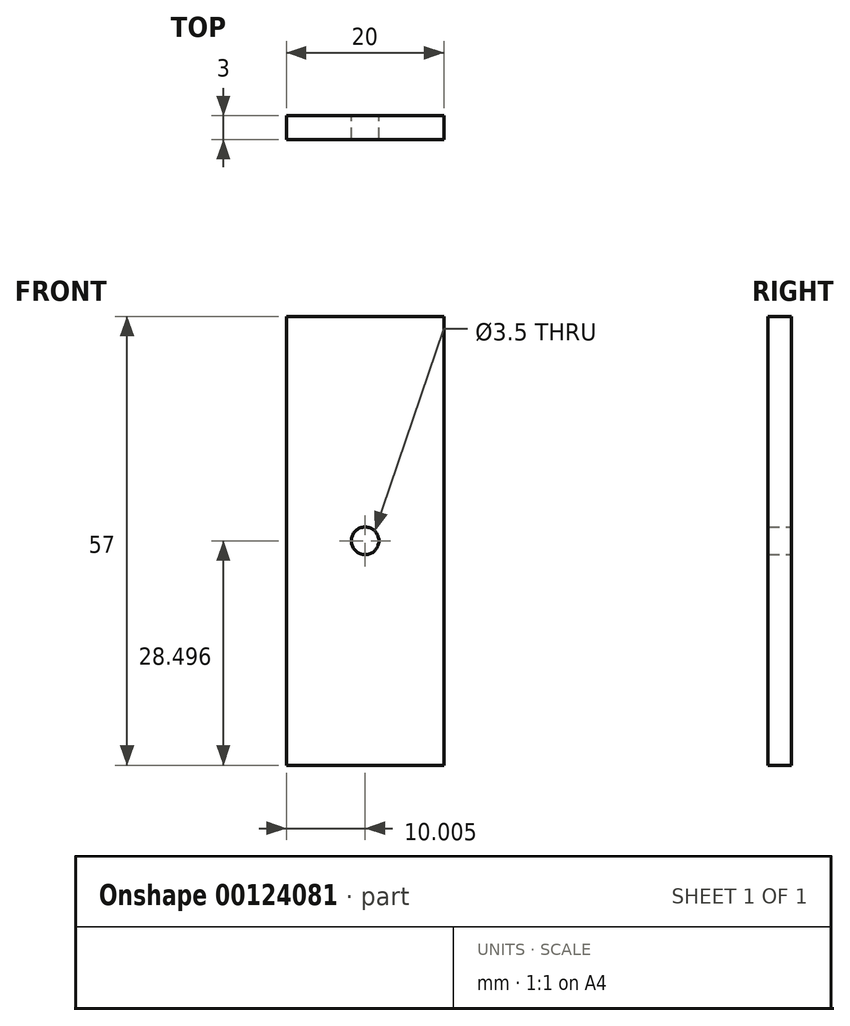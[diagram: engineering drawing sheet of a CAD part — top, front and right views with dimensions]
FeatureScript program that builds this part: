
annotation { "Feature Type Name" : "Feature", "Feature Type Description" : "" }
export const myFeature = defineFeature(function(context is Context, id is Id, definition is map)
    precondition{}
    {
        {
            var Q0;
            Q0=qCreatedBy(makeId("Front.planeOp"),FACE);
            var sketch = newSketch(context, id + "F0", { "sketchPlane" : qUnion([Q0])});
            skLineSegment(sketch, "E0.bottom", {"start": v(-40.73, 59.12) * mm, "end": v(-20.73, 59.12) * mm});
            skLineSegment(sketch, "E0.top", {"start": v(-40.73, 2.12) * mm, "end": v(-20.73, 2.12) * mm});
            skLineSegment(sketch, "E0.left", {"start": v(-40.73, 59.12) * mm, "end": v(-40.73, 2.12) * mm});
            skLineSegment(sketch, "E0.right", {"start": v(-20.73, 59.12) * mm, "end": v(-20.73, 2.12) * mm});
            skLineSegment(sketch, "E1", {"start": v(-30.73, 2.12) * mm, "end": v(-30.73, 59.12) * mm, "construction": true});
            skLineSegment(sketch, "E2", {"start": v(-40.73, 30.62) * mm, "end": v(-20.73, 30.62) * mm, "construction": true});
            skPoint(sketch, "E3", {"position": v(-30.73, 30.62) * mm});
            skCircle(sketch, "E4", {"center": v(-30.73, 30.62) * mm, "radius": 1.75 * mm});
            skSolve(sketch);
        }
        {
            var Q0;
            Q0 = qSketchRegion(id + "F0", true);
            extrude(context, id + "F1", {"entities" : qUnion([Q0]), "depth" : 3 * mm});
        }
    });
